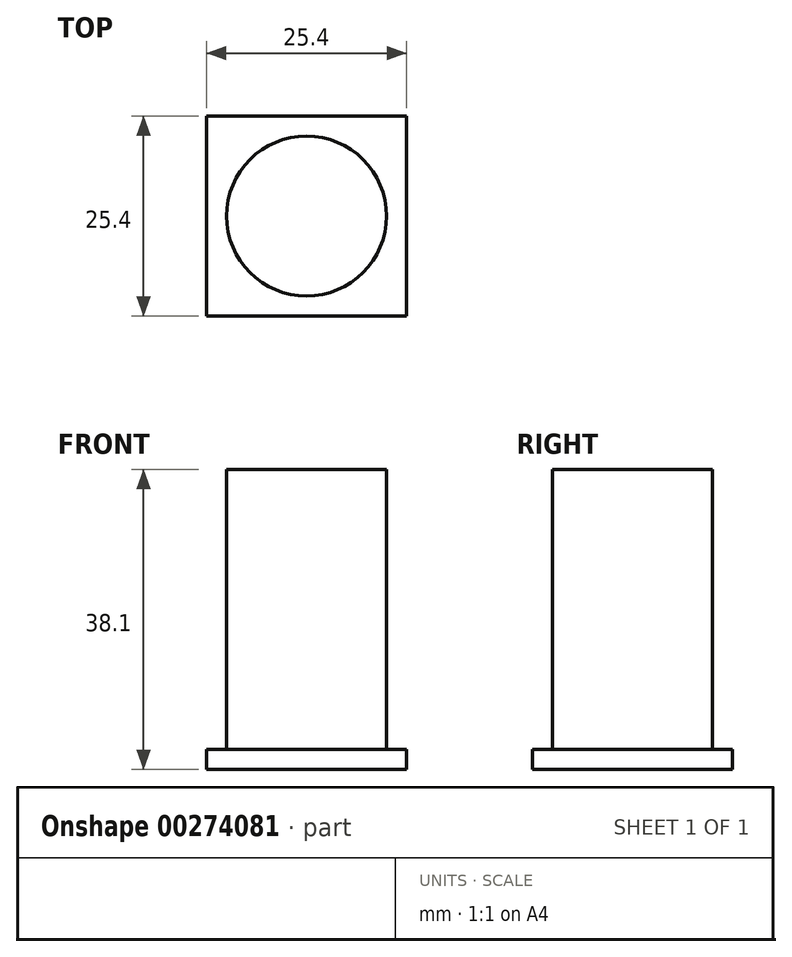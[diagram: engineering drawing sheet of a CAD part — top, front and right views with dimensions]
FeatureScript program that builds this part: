
annotation { "Feature Type Name" : "Feature", "Feature Type Description" : "" }
export const myFeature = defineFeature(function(context is Context, id is Id, definition is map)
    precondition{}
    {
        {
            var Q0;
            Q0=qCreatedBy(makeId("Top.planeOp"),FACE);
            var sketch = newSketch(context, id + "F0", { "sketchPlane" : qUnion([Q0])});
            skCircle(sketch, "E0", {"center": v(0, 0) * mm, "radius": 10.16 * mm});
            skSolve(sketch);
        }
        {
            var Q0;
            Q0 = qSketchRegion(id + "F0", true);
            extrude(context, id + "F1", {"entities" : qUnion([Q0]), "depth" : 38.1 * mm});
        }
        {
            var Q0;
            Q0=qCreatedBy(makeId("Top.planeOp"),FACE);
            var sketch = newSketch(context, id + "F2", { "sketchPlane" : qUnion([Q0])});
            skLineSegment(sketch, "E1.bottom", {"start": v(12.7, 12.7) * mm, "end": v(-12.7, 12.7) * mm});
            skLineSegment(sketch, "E1.top", {"start": v(12.7, -12.7) * mm, "end": v(-12.7, -12.7) * mm});
            skLineSegment(sketch, "E1.left", {"start": v(12.7, 12.7) * mm, "end": v(12.7, -12.7) * mm});
            skLineSegment(sketch, "E1.right", {"start": v(-12.7, 12.7) * mm, "end": v(-12.7, -12.7) * mm});
            skPoint(sketch, "E1.middle", {"position": v(0, 0) * mm});
            skSolve(sketch);
        }
        {
            var Q0;
            Q0=makeQuery(id+"F2.imprint","IMPRINT",FACE,{"disambiguationData":[TD([[makeQuery(id+"F2.imprint","IMPRINT",EDGE,{"derivedFrom":sQuery(id+"F2.wireOp",EDGE,"E1.bottom")}),1.0]])]});
            extrude(context, id + "F3", {"entities" : qUnion([Q0]), "operationType" : NewBodyOperationType.ADD, "depth" : 2.54 * mm});
        }
    });
